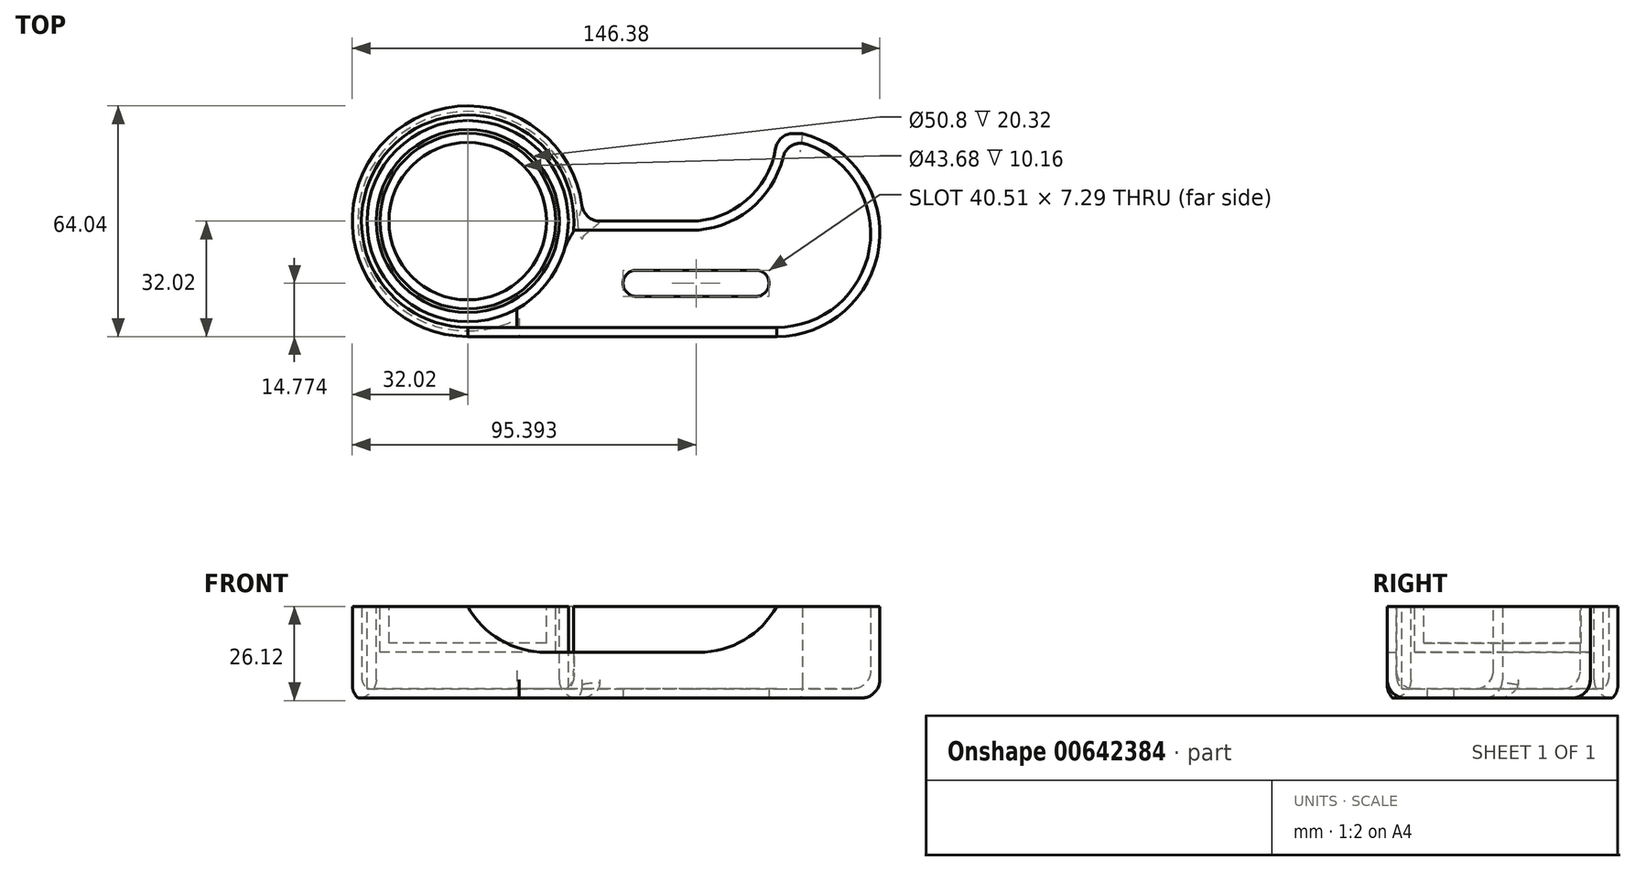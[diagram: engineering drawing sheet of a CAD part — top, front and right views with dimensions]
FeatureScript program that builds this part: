
annotation { "Feature Type Name" : "Feature", "Feature Type Description" : "" }
export const myFeature = defineFeature(function(context is Context, id is Id, definition is map)
    precondition{}
    {
        {
            var Q0;
            Q0=qCreatedBy(makeId("Top.planeOp"),FACE);
            var sketch = newSketch(context, id + "F0", { "sketchPlane" : qUnion([Q0])});
            skLineSegment(sketch, "E0", {"start": v(85.72, 24.36) * mm, "end": v(92.91, 24.36) * mm});
            skLineSegment(sketch, "E1", {"start": v(85.72, -32.02) * mm, "end": v(0, -32.02) * mm});
            skArc(sketch, "E2", {"start": v(0, -32.02) * mm, "mid": v(-32.02, 0) * mm, "end": v(0, 32.02) * mm});
            skArc(sketch, "E3", {"start": v(0, 32.02) * mm, "mid": v(22.64, 22.64) * mm, "end": v(32.02, 0) * mm});
            skLineSegment(sketch, "E4", {"start": v(32.02, 0) * mm, "end": v(61.73, 0) * mm});
            skArc(sketch, "E5", {"start": v(85.72, -32.02) * mm, "mid": v(114.13, -7) * mm, "end": v(92.91, 24.36) * mm});
            skArc(sketch, "E6", {"start": v(61.73, 0) * mm, "mid": v(78.82, 7.16) * mm, "end": v(85.72, 24.36) * mm});
            skSolve(sketch);
        }
        {
            var Q0;
            Q0 = qSketchRegion(id + "F0", true);
            extrude(context, id + "F1", {"entities" : qUnion([Q0]), "depth" : 25.4 * mm, "offsetDistance" : 25.4 * mm});
        }
        {
            var Q0;
            Q0=makeQuery(id+"F1.opExtrude","CAP_FACE",FACE,{"disambiguationData":[OSD([sQuery(id+"F0.wireOp",EDGE,"E0"),sQuery(id+"F0.wireOp",EDGE,"E1"),sQuery(id+"F0.wireOp",EDGE,"E2"),sQuery(id+"F0.wireOp",EDGE,"E3"),sQuery(id+"F0.wireOp",EDGE,"E4"),sQuery(id+"F0.wireOp",EDGE,"E5"),sQuery(id+"F0.wireOp",EDGE,"E6")])],"isStart":false});
            var sketch = newSketch(context, id + "F2", { "sketchPlane" : qUnion([Q0])});
            skCircle(sketch, "E7", {"center": v(0, 0) * mm, "radius": 25.4 * mm});
            skSolve(sketch);
        }
        {
            var Q0;
            Q0 = qSketchRegion(id + "F2", true);
            extrude(context, id + "F3", {"entities" : qUnion([Q0]), "operationType" : NewBodyOperationType.REMOVE, "endBound" : BoundingType.THROUGH_ALL, "oppositeDirection" : true, "depth" : 25.4 * mm, "offsetDistance" : 25.4 * mm});
        }
        {
            var Q0;
            Q0=makeQuery(id+"F1.opExtrude","CAP_FACE",FACE,{"disambiguationData":[OSD([sQuery(id+"F0.wireOp",EDGE,"E0"),sQuery(id+"F0.wireOp",EDGE,"E1"),sQuery(id+"F0.wireOp",EDGE,"E2"),sQuery(id+"F0.wireOp",EDGE,"E3"),sQuery(id+"F0.wireOp",EDGE,"E4"),sQuery(id+"F0.wireOp",EDGE,"E5"),sQuery(id+"F0.wireOp",EDGE,"E6")])],"isStart":false});
            shell(context, id + "F4", {"entities" : qUnion([Q0]), "thickness" : 2.54 * mm});
        }
        {
            var Q0;
            {var subQ0=sQuery(id+"F0.wireOp",EDGE,"E6");var subQ1=sQuery(id+"F0.wireOp",EDGE,"E5");var subQ2=sQuery(id+"F0.wireOp",EDGE,"E4");var subQ3=sQuery(id+"F0.wireOp",EDGE,"E3");var subQ4=sQuery(id+"F0.wireOp",EDGE,"E2");var subQ5=sQuery(id+"F0.wireOp",EDGE,"E1");var subQ6=sQuery(id+"F0.wireOp",EDGE,"E0");Q0=makeQuery(id+"F4.opShell","OFFSET_FACE",FACE,{"disambiguationData":[OSD([subQ6,subQ5,subQ4,subQ3,subQ2,subQ1,subQ0]),TDD([makeQuery(id+"F1.opExtrude","CAP_FACE",FACE,{"disambiguationData":[OSD([subQ6,subQ5,subQ4,subQ3,subQ2,subQ1,subQ0])],"isStart":false})])]});}
            var sketch = newSketch(context, id + "F5", { "sketchPlane" : qUnion([Q0])});
            skCircle(sketch, "E8", {"center": v(0, 0) * mm, "radius": 24.38 * mm});
            skSolve(sketch);
        }
        {
            var Q0;
            Q0 = qSketchRegion(id + "F5", true);
            extrude(context, id + "F6", {"entities" : qUnion([Q0]), "oppositeDirection" : true, "depth" : 12.7 * mm, "offsetDistance" : 25.4 * mm});
        }
        {
            var Q0;
            Q0=makeQuery(id+"F6.opExtrude","CAP_FACE",FACE,{"disambiguationData":[OSD([sQuery(id+"F5.wireOp",EDGE,"E8")])],"isStart":true});
            shell(context, id + "F7", {"entities" : qUnion([Q0]), "thickness" : 2.54 * mm});
        }
        {
            var Q0;
            Q0=makeQuery(id+"F1.opExtrude","SWEPT_FACE",FACE,{"disambiguationData":[OSD([sQuery(id+"F0.wireOp",EDGE,"E1")])]});
            var sketch = newSketch(context, id + "F8", { "sketchPlane" : qUnion([Q0])});
            skLineSegment(sketch, "E9.bottom", {"start": v(0, 25.4) * mm, "end": v(85.72, 25.4) * mm});
            skLineSegment(sketch, "E9.top", {"start": v(0, 12.7) * mm, "end": v(85.72, 12.7) * mm});
            skLineSegment(sketch, "E9.left", {"start": v(0, 25.4) * mm, "end": v(0, 12.7) * mm});
            skLineSegment(sketch, "E9.right", {"start": v(85.72, 25.4) * mm, "end": v(85.72, 12.7) * mm});
            skSolve(sketch);
        }
        {
            var Q0;
            Q0=makeQuery(id+"F8.imprint","IMPRINT",FACE,{"disambiguationData":[TD([[makeQuery(id+"F8.imprint","IMPRINT",EDGE,{"derivedFrom":sQuery(id+"F8.wireOp",EDGE,"E9.bottom")}),1.0]])]});
            extrude(context, id + "F9", {"entities" : qUnion([Q0]), "operationType" : NewBodyOperationType.REMOVE, "oppositeDirection" : true, "depth" : 3.8 * mm, "offsetDistance" : 25.4 * mm});
        }
        {
            var Q0;
            Q0=makeQuery(id+"F9.boolean.opBoolean","COPY",EDGE,{"derivedFrom":makeQuery(id+"F9.opExtrude","SWEPT_EDGE",EDGE,{"disambiguationData":[OSD([sQuery(id+"F0.wireOp",EDGE,"E1"),sQuery(id+"F0.wireOp",EDGE,"E5"),sQuery(id+"F8.wireOp",EDGE,"E9.top"),sQuery(id+"F8.wireOp",EDGE,"E9.right")])]})});
            fillet(context, id + "F10", {"entities" : qUnion([Q0]), "radius" : 24.53 * mm, "tangentPropagation" : true, "allowEdgeOverflow" : false});
        }
        {
            var Q0;
            Q0=makeQuery(id+"F9.boolean.opBoolean","COPY",EDGE,{"derivedFrom":makeQuery(id+"F9.opExtrude","SWEPT_EDGE",EDGE,{"disambiguationData":[OSD([sQuery(id+"F0.wireOp",EDGE,"E1"),sQuery(id+"F0.wireOp",EDGE,"E2"),sQuery(id+"F8.wireOp",EDGE,"E9.top"),sQuery(id+"F8.wireOp",EDGE,"E9.left")])]})});
            fillet(context, id + "F11", {"entities" : qUnion([Q0]), "radius" : 24.84 * mm, "tangentPropagation" : true, "allowEdgeOverflow" : false});
        }
        {
            var Q0;
            Q0=makeQuery(id+"F3.boolean.opBoolean","INTERSECT",EDGE,{"derivedFrom":[makeQuery(id+"F1.opExtrude","CAP_FACE",FACE,{"disambiguationData":[OSD([sQuery(id+"F0.wireOp",EDGE,"E0"),sQuery(id+"F0.wireOp",EDGE,"E1"),sQuery(id+"F0.wireOp",EDGE,"E2"),sQuery(id+"F0.wireOp",EDGE,"E3"),sQuery(id+"F0.wireOp",EDGE,"E4"),sQuery(id+"F0.wireOp",EDGE,"E5"),sQuery(id+"F0.wireOp",EDGE,"E6")])],"isStart":true}),makeQuery(id+"F3.opExtrude","SWEPT_FACE",FACE,{"disambiguationData":[OSD([sQuery(id+"F2.wireOp",EDGE,"E7")])]})]});
            fillet(context, id + "F12", {"entities" : qUnion([Q0]), "radius" : 5.08 * mm, "tangentPropagation" : true, "allowEdgeOverflow" : false});
        }
        {
            var Q0;
            {var subQ0=sQuery(id+"F0.wireOp",EDGE,"E5");Q0=makeQuery(id+"F4.opShell","OFFSET_EDGE",EDGE,{"disambiguationData":[OSD([subQ0]),TDD([makeQuery(id+"F1.opExtrude","CAP_EDGE",EDGE,{"disambiguationData":[OSD([subQ0])],"isStart":true})])]});}
            fillet(context, id + "F13", {"entities" : qUnion([Q0]), "radius" : 5.08 * mm, "tangentPropagation" : true, "allowEdgeOverflow" : false});
        }
        {
            var Q0;
            {var subQ0=sQuery(id+"F0.wireOp",EDGE,"E4");Q0=makeQuery(id+"F4.opShell","OFFSET_EDGE",EDGE,{"disambiguationData":[OSD([subQ0]),TDD([makeQuery(id+"F1.opExtrude","CAP_EDGE",EDGE,{"disambiguationData":[OSD([subQ0])],"isStart":true})])]});}
            fillet(context, id + "F14", {"entities" : qUnion([Q0]), "radius" : 5.08 * mm, "tangentPropagation" : true, "allowEdgeOverflow" : false});
        }
        {
            var Q0;
            Q0=makeQuery(id+"F1.opExtrude","CAP_EDGE",EDGE,{"disambiguationData":[OSD([sQuery(id+"F0.wireOp",EDGE,"E6")])],"isStart":true});
            var Q1;
            Q1=makeQuery(id+"F1.opExtrude","CAP_EDGE",EDGE,{"disambiguationData":[OSD([sQuery(id+"F0.wireOp",EDGE,"E4")])],"isStart":true});
            fillet(context, id + "F15", {"entities" : qUnion([Q0, Q1]), "radius" : 5.08 * mm, "tangentPropagation" : true, "allowEdgeOverflow" : false});
        }
        {
            var Q0;
            Q0=makeQuery(id+"F1.opExtrude","CAP_EDGE",EDGE,{"disambiguationData":[OSD([sQuery(id+"F0.wireOp",EDGE,"E5")])],"isStart":true});
            var Q1;
            Q1=makeQuery(id+"F15.opFillet","BLEND_EDGE",EDGE,{"blendedFrom":[makeQuery(id+"F1.opExtrude","CAP_EDGE",EDGE,{"disambiguationData":[OSD([sQuery(id+"F0.wireOp",EDGE,"E6")])],"isStart":true}),makeQuery(id+"F1.opExtrude","SWEPT_FACE",FACE,{"disambiguationData":[OSD([sQuery(id+"F0.wireOp",EDGE,"E0")])]})],"blendedInto":[makeQuery(id+"F1.opExtrude","SWEPT_FACE",FACE,{"disambiguationData":[OSD([sQuery(id+"F0.wireOp",EDGE,"E0")])]})]});
            fillet(context, id + "F16", {"entities" : qUnion([Q0, Q1]), "radius" : 5.08 * mm, "tangentPropagation" : true, "allowEdgeOverflow" : false});
        }
        {
            var Q0;
            Q0=makeQuery(id+"F1.opExtrude","SWEPT_EDGE",EDGE,{"disambiguationData":[OSD([sQuery(id+"F0.wireOp",EDGE,"E3"),sQuery(id+"F0.wireOp",EDGE,"E4")])]});
            fillet(context, id + "F17", {"entities" : qUnion([Q0]), "radius" : 5.08 * mm, "tangentPropagation" : true, "allowEdgeOverflow" : false});
        }
        {
            var Q0;
            Q0=makeQuery(id+"F1.opExtrude","CAP_FACE",FACE,{"disambiguationData":[OSD([sQuery(id+"F0.wireOp",EDGE,"E0"),sQuery(id+"F0.wireOp",EDGE,"E1"),sQuery(id+"F0.wireOp",EDGE,"E2"),sQuery(id+"F0.wireOp",EDGE,"E3"),sQuery(id+"F0.wireOp",EDGE,"E4"),sQuery(id+"F0.wireOp",EDGE,"E5"),sQuery(id+"F0.wireOp",EDGE,"E6")])],"isStart":true});
            var sketch = newSketch(context, id + "F18", { "sketchPlane" : qUnion([Q0])});
            skLineSegment(sketch, "E10.bottom", {"start": v(46.76, 20.9) * mm, "end": v(79.98, 20.9) * mm});
            skLineSegment(sketch, "E10.top", {"start": v(46.76, 13.6) * mm, "end": v(79.98, 13.6) * mm});
            skLineSegment(sketch, "E10.left", {"start": v(46.76, 20.9) * mm, "end": v(46.76, 13.6) * mm});
            skLineSegment(sketch, "E10.right", {"start": v(79.98, 20.9) * mm, "end": v(79.98, 13.6) * mm});
            skArc(sketch, "E11", {"start": v(79.98, 13.6) * mm, "mid": v(83.63, 17.25) * mm, "end": v(79.98, 20.9) * mm});
            skArc(sketch, "E12", {"start": v(46.76, 20.9) * mm, "mid": v(43.12, 17.25) * mm, "end": v(46.76, 13.6) * mm});
            skSolve(sketch);
        }
        {
            var Q0;
            Q0=makeQuery(id+"F18.imprint","IMPRINT",FACE,{"disambiguationData":[TD([[makeQuery(id+"F18.imprint","IMPRINT",EDGE,{"derivedFrom":sQuery(id+"F18.wireOp",EDGE,"E10.left")}),-1.0]])]});
            var Q1;
            Q1=makeQuery(id+"F18.imprint","IMPRINT",FACE,{"disambiguationData":[TD([[makeQuery(id+"F18.imprint","IMPRINT",EDGE,{"derivedFrom":sQuery(id+"F18.wireOp",EDGE,"E10.right")}),1.0]])]});
            var Q2;
            Q2=makeQuery(id+"F18.imprint","IMPRINT",FACE,{"disambiguationData":[TD([[makeQuery(id+"F18.imprint","IMPRINT",EDGE,{"derivedFrom":sQuery(id+"F18.wireOp",EDGE,"E10.bottom")}),-1.0]])]});
            extrude(context, id + "F19", {"entities" : qUnion([Q0, Q1, Q2]), "operationType" : NewBodyOperationType.REMOVE, "oppositeDirection" : true, "depth" : 25.4 * mm, "offsetDistance" : 25.4 * mm});
        }
    });
